# Revit family: Тактильная плитка ПВХ линейное расположение (приклеивание)
name_source: partatom
category: Оборудование
revit_build: Autodesk Revit 2017 (Build: 20160225_1515(x64)
units: mm (PartAtom-declared; Revit-internal decimal feet)

## family parameters
Общий = Да
Основа = Грань
При загрузке вырезать с полостями = Да
Размер круглого соединителя = Использовать диаметр
Тип детали = Нормальный
Точка расчета площади = Нет

## types (2) — shared parameters
ADSK_Наименование = Тактильная плитка ПВХ линейное расположение (приклеивание)
ADSK_Размер_Высота рифа = 5 мм
ADSK_Размер_Габариты = 300Х300
ADSK_Размер_Длина = 300 мм
ADSK_Размер_Толщина = 2 мм
ADSK_Размер_Ширина = 300 мм
ADSK_Тип рифов = Конусообразные рифы, линейное расположение
URL = http://tiflocentre.ru
Изготовитель = ТИФЛОЦЕНТР «ВЕРТИКАЛЬ»
Применение = Улица/Помещение
Стоимость = 175 $
zero-valued in all types: Отметка по умолчанию

## per-type parameters (varying)
| type | ADSK_Код изделия | ADSK_Материал наименование | ADSK_Материал плитки | Описание |
| Тактильная плитка полиуретан дагональ_Желтая | 10653-ZH | Полиуретан, цвет желтый | Вертикаль_Полиуретан_Желтый | Тактильная плитка ПВХ с тактильными конусами в линейном порядке информирует человека с ограничениями зрения о преодолимом препятствии на пути. Желтый цвет служит контрастом к темной поверхности, что особенно важно для слабовидящего человека. Особенность данной серии ПВХ плитки - самоклеящаяс основа, позволяющая ее легко монтировать в помещениях. Самоклеящаяся плитка ПВХ протестирована незрячими специалистами и рекомендована к применению ВОС. |
| Тактильная плитка полиуретановая_Черная | 10653-CH | Полиуретан, цвет черный | Вертикаль_Полиуретан_Черный | Тактильная плитка ПВХ с тактильными конусами в линейном порядке информирует человека с ограничениями зрения о преодолимом препятствии на пути. При этом черный цвет плитки является контрастом к светлой поверхности, что особенно важно для слабовидящего человека. Данную ПВХ плитку очень легко монтировать внутри помещений методом приклеивания. |
